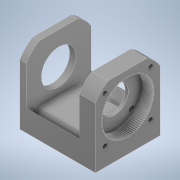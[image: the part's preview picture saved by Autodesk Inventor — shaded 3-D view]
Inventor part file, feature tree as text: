
AUTODESK INVENTOR PART (.ipt)
format: ipt  version: 2022 (Build 260153000, 153)  size: 678,400 bytes
history: mixed  units: in
note: dims shown in document units (in); Inventor stores cm internally (conversion verified against a paired STEP export)
features: extrude x9, sketch x9, plane x1, other x1, imported_body x1
ambient origin geometry x8: Origin, YZ Plane, XZ Plane, XY Plane, X Axis, Y Axis, Z Axis, Center Point
bodies: Solid1 (imported_parasolid)
feature tree (21):
  extrude  "Extrusion1"  Depth=0.3937in TaperAngle=0.0deg
  plane  "Work Plane1"
  extrude  "Extrusion2"  Depth=0.9843in TaperAngle=0.0deg
  extrude  "Extrusion5"  TaperAngle=0.0deg  [1 undecoded]
  extrude  "Extrusion6"  Depth=0.5906in TaperAngle=0.0deg
  extrude  "Extrusion7"  Depth=0.0984in
  extrude  "Extrusion8"  Depth=0.3937in TaperAngle=0.0deg
  extrude  "Extrusion9"  Depth=0.2362in TaperAngle=0.0deg
  extrude  "Extrusion10"  Depth=0.0197in
  extrude  "Extrusion11"  [1 undecoded]
  sketch  "Sketch2"  dims[d1=0.3937in d2=0.0in d3=0.3937in d4=0.0in]
  sketch  "Sketch3"  dims[d9=0.2756in d10=0.9843in d11=0.0in]
  sketch  "Sketch6"  dims[d12=0.7874in d13=0.0in d14=0.0in]
  sketch  "Sketch7"  dims[d15=0.5906in d16=0.0in d17=1.1811in d18=0.0in]
  sketch  "Sketch8"  dims[d19=0.5906in d20=0.0in d25=0.0984in]
  sketch  "Sketch9"  dims[d26=0.0984in d27=0.3937in d28=0.0in]
  sketch  "Sketch10"  dims[d29=1.2697in d30=0.2362in d31=0.0in]
  sketch  "Sketch11"  dims[d7=0.0197in d8=0.0344in]
  sketch  "Sketch12"
  other  "96_Teeth_Gear.STEP"
  imported_body  NMx_Import_Brep_tag  [imported B-rep: ~433 faces, bbox_mm=[70.0, 68.027756, 60.0]]
note: 2 required parameter values undecoded (feature->parameter linkage not recoverable at this tier; creation-order binding heuristic only, values carry confidence <= 0.55)
